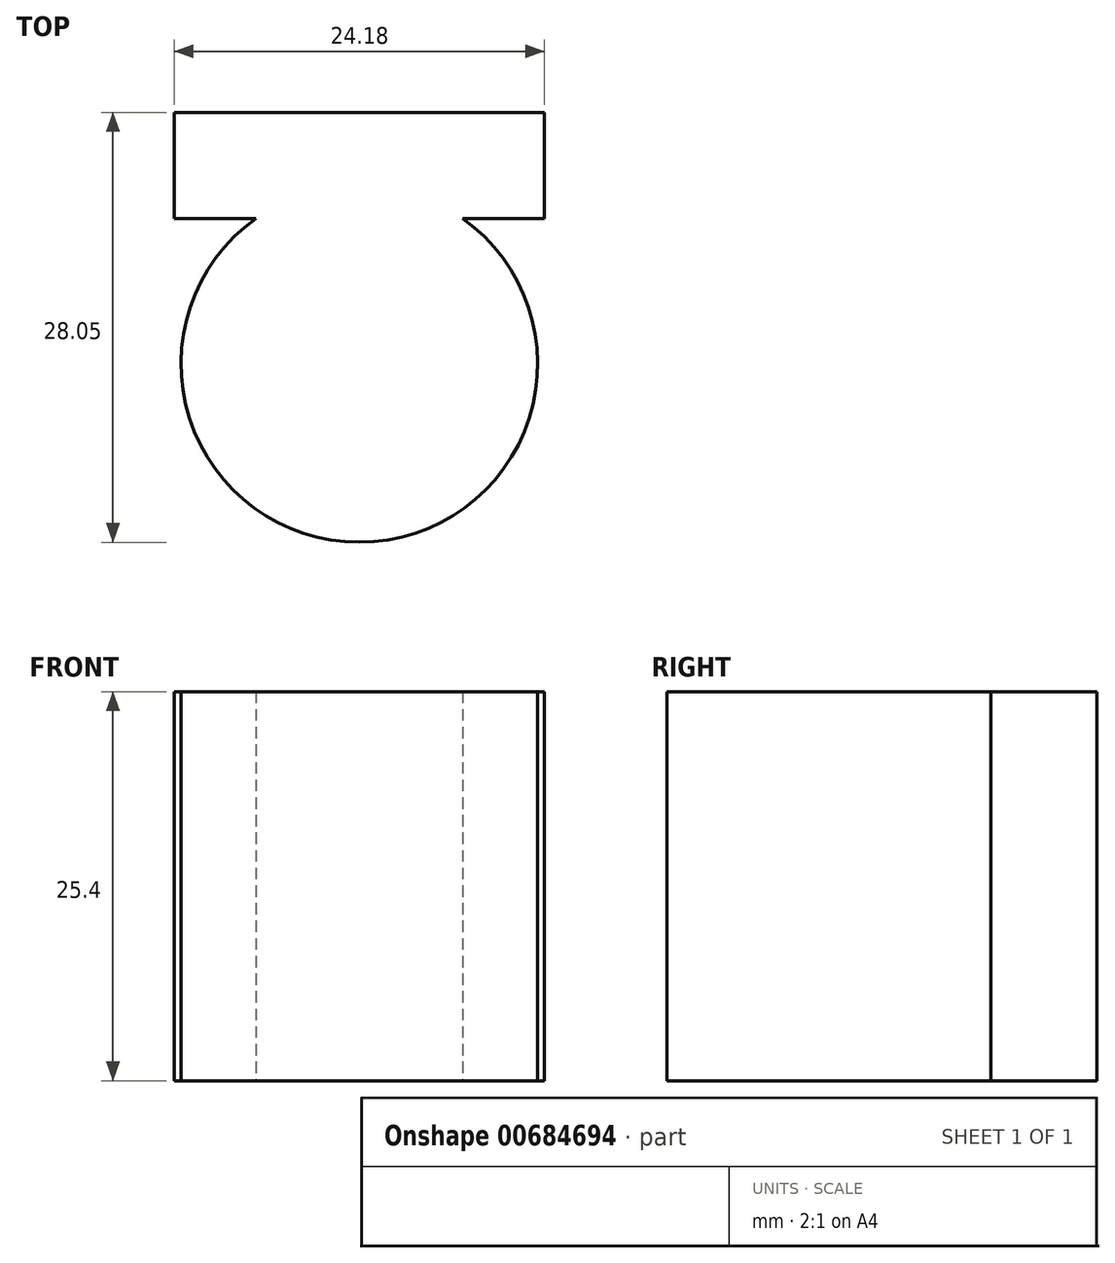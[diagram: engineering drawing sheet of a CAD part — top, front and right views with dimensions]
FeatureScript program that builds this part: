
annotation { "Feature Type Name" : "Feature", "Feature Type Description" : "" }
export const myFeature = defineFeature(function(context is Context, id is Id, definition is map)
    precondition{}
    {
        {
            var Q0;
            Q0=qCreatedBy(makeId("Top.planeOp"),FACE);
            var sketch = newSketch(context, id + "F0", { "sketchPlane" : qUnion([Q0])});
            skCircle(sketch, "E0", {"center": v(-36.12, 22.3) * mm, "radius": 11.64 * mm});
            skLineSegment(sketch, "E1.bottom", {"start": v(-48.2, 38.7) * mm, "end": v(-24.03, 38.7) * mm});
            skLineSegment(sketch, "E1.top", {"start": v(-48.2, 31.8) * mm, "end": v(-24.03, 31.8) * mm});
            skLineSegment(sketch, "E1.left", {"start": v(-48.2, 38.7) * mm, "end": v(-48.2, 31.8) * mm});
            skLineSegment(sketch, "E1.right", {"start": v(-24.03, 38.7) * mm, "end": v(-24.03, 31.8) * mm});
            skSolve(sketch);
        }
        {
            var Q0;
            Q0=qSketchRegion(id+"F0",true);
            extrude(context, id + "F1", {"entities" : qUnion([Q0]), "depth" : 25.4 * mm, "offsetDistance" : 25.4 * mm});
        }
    });
